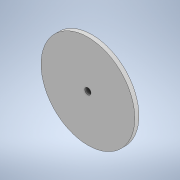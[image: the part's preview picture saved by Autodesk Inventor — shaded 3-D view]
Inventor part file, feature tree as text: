
AUTODESK INVENTOR PART (.ipt)
format: ipt  version: 2021 (Build 250183000, 183)  size: 103,936 bytes
history: native  units: mm
features: extrude x2, sketch x2, thread x1
ambient origin geometry x8: Origin, YZ Plane, XZ Plane, XY Plane, X Axis, Y Axis, Z Axis, Center Point
bodies: Solid1 (feature_tree)
feature tree (5):
  extrude  "Extrusion1"  TaperAngle=0.0deg  [1 undecoded]
  extrude  "Extrusion2"  Depth=4.0mm TaperAngle=0.0deg
  thread  "Thread1"  [1 undecoded]
  sketch  "Sketch1"  dims[d0=0.0mm d1=0.0mm]
  sketch  "Sketch2"  dims[d2=90.0mm d3=4.0mm d4=0.0mm d5=6.0mm d6=9.0mm d7=0.0mm d8=4.0mm d9=0.0mm d10=0.5mm d11=0.872665mm d12=0.5mm d13=0.872665mm]
note: 2 required parameter values undecoded (feature->parameter linkage not recoverable at this tier; creation-order binding heuristic only, values carry confidence <= 0.55)
